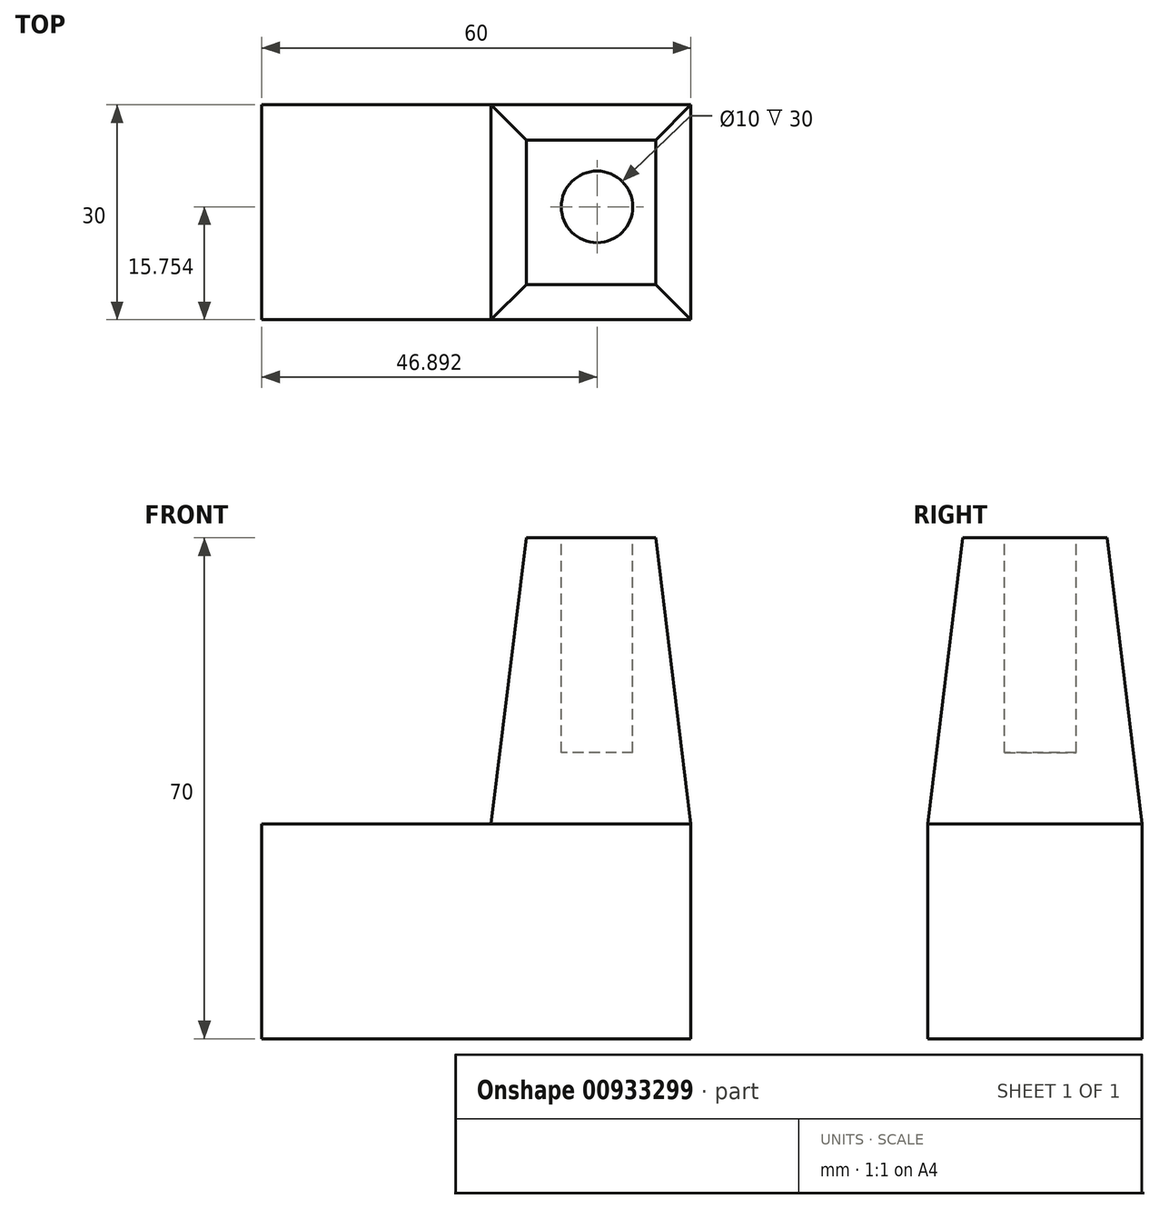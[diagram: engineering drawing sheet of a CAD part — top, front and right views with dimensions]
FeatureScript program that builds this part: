
annotation { "Feature Type Name" : "Feature", "Feature Type Description" : "" }
export const myFeature = defineFeature(function(context is Context, id is Id, definition is map)
    precondition{}
    {
        {
            var Q0;
            Q0=qCreatedBy(makeId("Front.planeOp"),FACE);
            var sketch = newSketch(context, id + "F0", { "sketchPlane" : qUnion([Q0])});
            skLineSegment(sketch, "E0.bottom", {"start": v(-32.07, 16.25) * mm, "end": v(27.93, 16.25) * mm});
            skLineSegment(sketch, "E0.top", {"start": v(-32.07, -13.75) * mm, "end": v(27.93, -13.75) * mm});
            skLineSegment(sketch, "E0.left", {"start": v(-32.07, 16.25) * mm, "end": v(-32.07, -13.75) * mm});
            skLineSegment(sketch, "E0.right", {"start": v(27.93, 16.25) * mm, "end": v(27.93, -13.75) * mm});
            skSolve(sketch);
        }
        {
            var Q0;
            Q0=makeQuery(id+"F0.imprint","IMPRINT",FACE,{"disambiguationData":[TD([[makeQuery(id+"F0.imprint","IMPRINT",EDGE,{"derivedFrom":sQuery(id+"F0.wireOp",EDGE,"E0.bottom")}),-1.0]])]});
            extrude(context, id + "F1", {"entities" : qUnion([Q0]), "depth" : 30 * mm, "offsetDistance" : 25.4 * mm});
        }
        {
            var Q0;
            Q0=makeQuery(id+"F1.opExtrude","SWEPT_FACE",FACE,{"disambiguationData":[OSD([sQuery(id+"F0.wireOp",EDGE,"E0.bottom")])]});
            var sketch = newSketch(context, id + "F2", { "sketchPlane" : qUnion([Q0])});
            skLineSegment(sketch, "E1.bottom", {"start": v(27.93, 0) * mm, "end": v(0, 0) * mm});
            skLineSegment(sketch, "E1.top", {"start": v(27.93, -30) * mm, "end": v(0, -30) * mm});
            skLineSegment(sketch, "E1.left", {"start": v(27.93, 0) * mm, "end": v(27.93, -30) * mm});
            skLineSegment(sketch, "E1.right", {"start": v(0, 0) * mm, "end": v(0, -30) * mm});
            skSolve(sketch);
        }
        {
            var Q0;
            Q0=makeQuery(id+"F2.imprint","IMPRINT",FACE,{"disambiguationData":[TD([[makeQuery(id+"F2.imprint","IMPRINT",EDGE,{"derivedFrom":sQuery(id+"F2.wireOp",EDGE,"E1.bottom")}),-1.0]])]});
            extrude(context, id + "F3", {"entities" : qUnion([Q0]), "operationType" : NewBodyOperationType.ADD, "depth" : 40 * mm, "offsetDistance" : 25.4 * mm, "hasDraft" : true, "draftAngle" : 7 * degree, "draftPullDirection" : true});
        }
        {
            var Q0;
            Q0=makeQuery(id+"F3.opExtrude","CAP_FACE",FACE,{"disambiguationData":[OSD([sQuery(id+"F2.wireOp",EDGE,"E1.bottom"),sQuery(id+"F2.wireOp",EDGE,"E1.top"),sQuery(id+"F2.wireOp",EDGE,"E1.left"),sQuery(id+"F2.wireOp",EDGE,"E1.right")])],"isStart":false});
            var sketch = newSketch(context, id + "F4", { "sketchPlane" : qUnion([Q0])});
            skCircle(sketch, "E2", {"center": v(14.82, -14.25) * mm, "radius": 5 * mm});
            skSolve(sketch);
        }
        {
            var Q0;
            Q0 = qSketchRegion(id + "F4", true);
            extrude(context, id + "F5", {"entities" : qUnion([Q0]), "operationType" : NewBodyOperationType.REMOVE, "oppositeDirection" : true, "depth" : 30 * mm, "offsetDistance" : 25.4 * mm});
        }
    });
